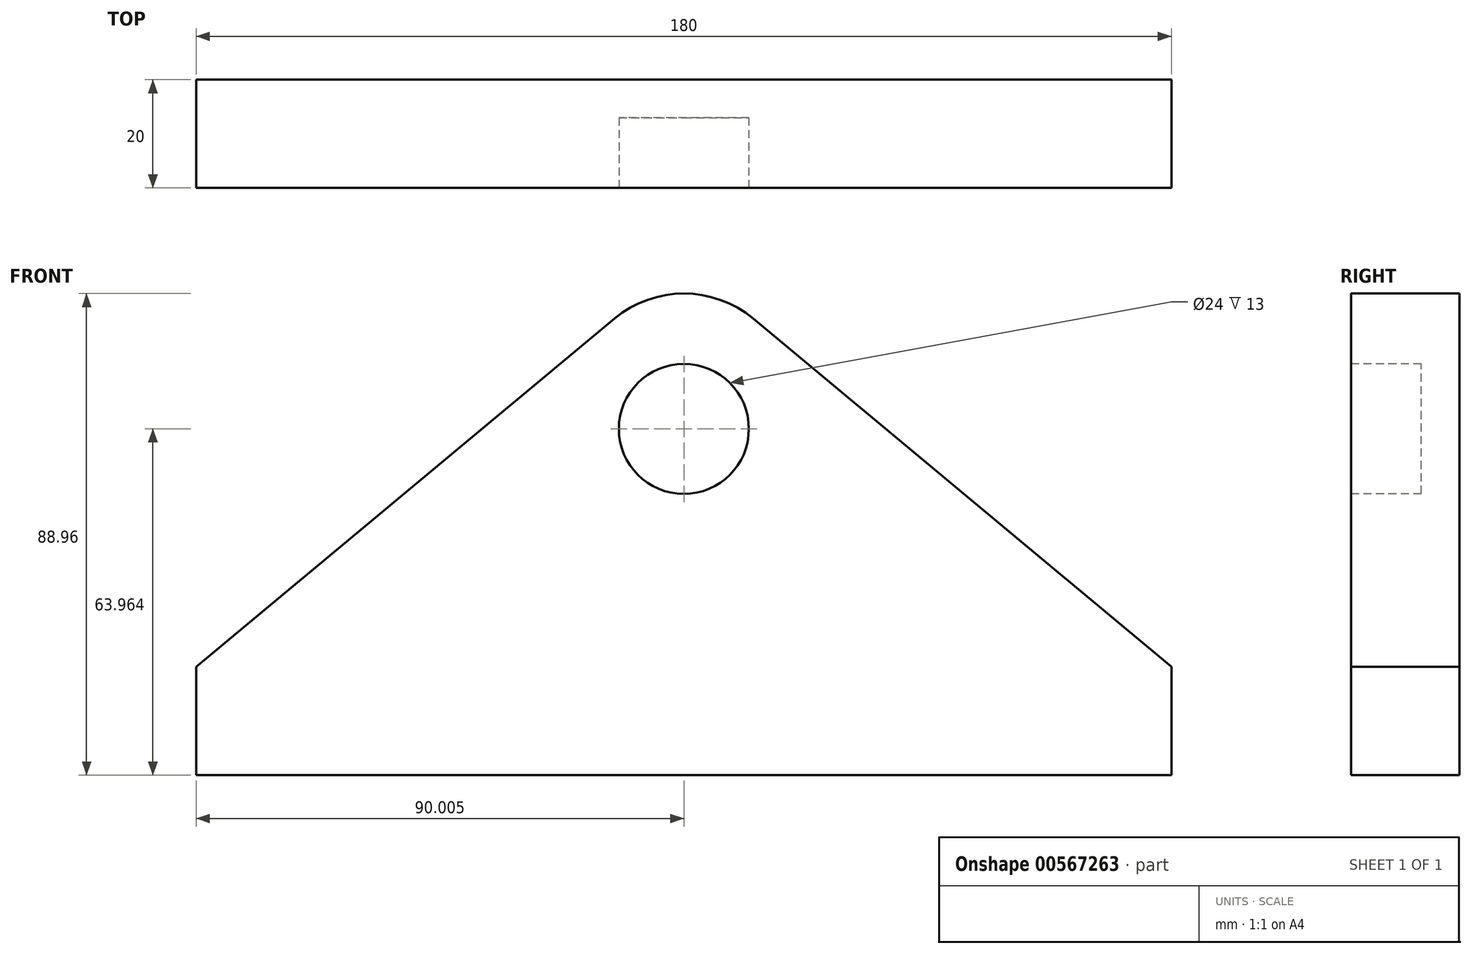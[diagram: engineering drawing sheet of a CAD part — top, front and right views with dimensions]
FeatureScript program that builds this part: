
annotation { "Feature Type Name" : "Feature", "Feature Type Description" : "" }
export const myFeature = defineFeature(function(context is Context, id is Id, definition is map)
    precondition{}
    {
        {
            var Q0;
            Q0=qCreatedBy(makeId("Front.planeOp"),FACE);
            var sketch = newSketch(context, id + "F0", { "sketchPlane" : qUnion([Q0])});
            skLineSegment(sketch, "E0.top", {"start": v(-98.78, -29.2) * mm, "end": v(81.22, -29.2) * mm});
            skLineSegment(sketch, "E1", {"start": v(81.22, 70.8) * mm, "end": v(81.22, 65.8) * mm});
            skLineSegment(sketch, "E2", {"start": v(-98.78, -29.2) * mm, "end": v(-98.78, -9.2) * mm});
            skLineSegment(sketch, "E3", {"start": v(81.22, -29.2) * mm, "end": v(81.22, -9.2) * mm});
            skLineSegment(sketch, "E4", {"start": v(-98.78, -9.2) * mm, "end": v(-21.58, 55.14) * mm});
            skLineSegment(sketch, "E5", {"start": v(4.03, 55.14) * mm, "end": v(81.22, -9.2) * mm});
            skPoint(sketch, "E6.visualSharp", {"position": v(-8.78, 65.8) * mm});
            skArc(sketch, "E6.filletArc", {"start": v(4.03, 55.14) * mm, "mid": v(-8.78, 59.77) * mm, "end": v(-21.58, 55.14) * mm});
            skLineSegment(sketch, "E7", {"start": v(-8.78, 59.77) * mm, "end": v(-8.78, 34.77) * mm});
            skSolve(sketch);
        }
        {
            var Q0;
            Q0 = qSketchRegion(id + "F0", true);
            extrude(context, id + "F1", {"entities" : qUnion([Q0]), "depth" : 20 * mm, "offsetDistance" : 25 * mm});
        }
        {
            var Q0;
            Q0=makeQuery(id+"F1.opExtrude","CAP_FACE",FACE,{"disambiguationData":[OSD([sQuery(id+"F0.wireOp",EDGE,"E0.top"),sQuery(id+"F0.wireOp",EDGE,"E2"),sQuery(id+"F0.wireOp",EDGE,"E3"),sQuery(id+"F0.wireOp",EDGE,"E4"),sQuery(id+"F0.wireOp",EDGE,"E5"),sQuery(id+"F0.wireOp",EDGE,"E6.filletArc")])],"isStart":false});
            var sketch = newSketch(context, id + "F2", { "sketchPlane" : qUnion([Q0])});
            skLineSegment(sketch, "E8", {"start": v(-8.78, 59.77) * mm, "end": v(-8.78, 34.77) * mm});
            skCircle(sketch, "E9", {"center": v(-8.78, 34.77) * mm, "radius": 12 * mm});
            skSolve(sketch);
        }
        {
            var Q0;
            Q0=makeQuery(id+"F2.imprint","IMPRINT",FACE,{"disambiguationData":[TD([[makeQuery(id+"F2.imprint","IMPRINT",EDGE,{"derivedFrom":sQuery(id+"F2.wireOp",EDGE,"E9")}),1.0]])]});
            extrude(context, id + "F3", {"entities" : qUnion([Q0]), "operationType" : NewBodyOperationType.REMOVE, "oppositeDirection" : true, "depth" : 13 * mm, "offsetDistance" : 25 * mm});
        }
    });
